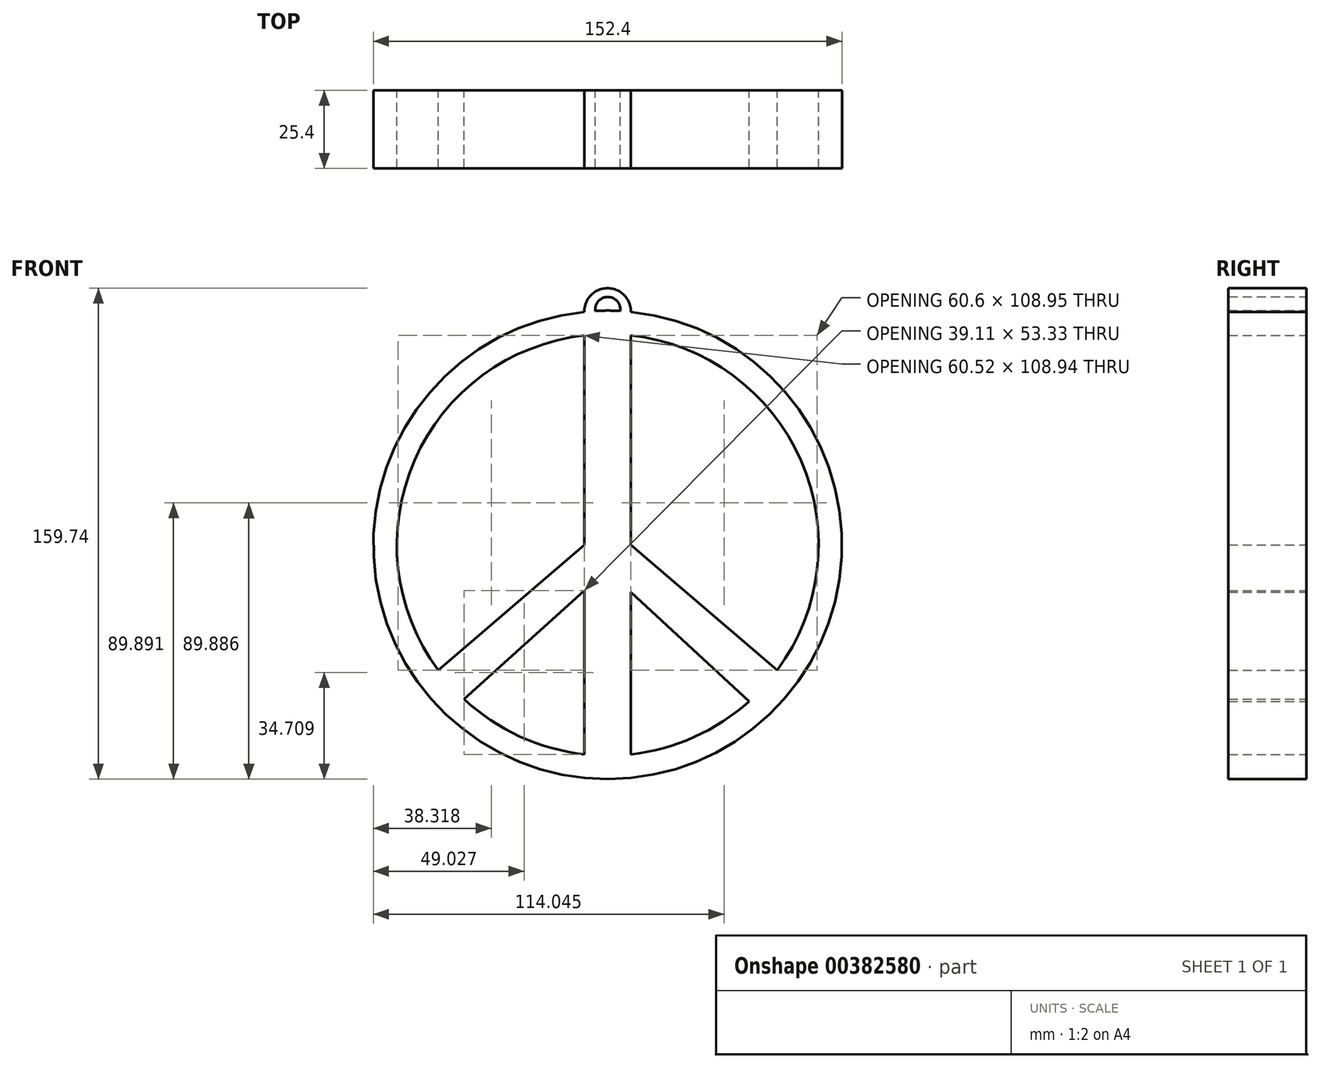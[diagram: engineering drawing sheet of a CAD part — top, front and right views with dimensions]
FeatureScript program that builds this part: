
annotation { "Feature Type Name" : "Feature", "Feature Type Description" : "" }
export const myFeature = defineFeature(function(context is Context, id is Id, definition is map)
    precondition{}
    {
        {
            var Q0;
            Q0=qCreatedBy(makeId("Front.planeOp"),FACE);
            var sketch = newSketch(context, id + "F0", { "sketchPlane" : qUnion([Q0])});
            skArc(sketch, "E0", {"start": v(-7.62, 75.82) * mm, "mid": v(0.04, -76.2) * mm, "end": v(7.54, 75.83) * mm});
            skLineSegment(sketch, "E1", {"start": v(7.54, 68.16) * mm, "end": v(7.54, 0) * mm});
            skLineSegment(sketch, "E2", {"start": v(-7.62, 68.16) * mm, "end": v(-7.62, 0) * mm});
            skLineSegment(sketch, "E3", {"start": v(-7.62, 0) * mm, "end": v(-55.14, -40.78) * mm});
            skLineSegment(sketch, "E4", {"start": v(55.14, -40.78) * mm, "end": v(7.54, 0) * mm});
            skLineSegment(sketch, "E5.trimOffspring", {"start": v(7.54, -15.38) * mm, "end": v(7.54, -68.16) * mm});
            skLineSegment(sketch, "E6.trimOffspring", {"start": v(-7.62, -14.83) * mm, "end": v(-7.62, -68.16) * mm});
            skArc(sketch, "E7", {"start": v(-46.73, -50.2) * mm, "mid": v(-28.62, -62.32) * mm, "end": v(-7.62, -68.16) * mm});
            skArc(sketch, "E8.trimOffspring", {"start": v(7.54, -68.16) * mm, "mid": v(28.1, -62.56) * mm, "end": v(45.95, -50.91) * mm});
            skArc(sketch, "E9.trimOffspring", {"start": v(55.14, -40.78) * mm, "mid": v(62.85, 27.45) * mm, "end": v(7.54, 68.16) * mm});
            skArc(sketch, "E10.trimOffspring", {"start": v(-7.62, 68.16) * mm, "mid": v(-62.86, 27.42) * mm, "end": v(-55.14, -40.78) * mm});
            skLineSegment(sketch, "E11", {"start": v(-7.62, -14.83) * mm, "end": v(-46.73, -50.2) * mm});
            skLineSegment(sketch, "E12", {"start": v(7.54, -15.38) * mm, "end": v(45.95, -50.91) * mm});
            skArc(sketch, "E13", {"start": v(7.54, 75.83) * mm, "mid": v(-0.04, 83.54) * mm, "end": v(-7.62, 75.82) * mm});
            skArc(sketch, "E14", {"start": v(4.06, 76.1) * mm, "mid": v(0.04, 80.7) * mm, "end": v(-4, 76.1) * mm});
            skArc(sketch, "E15", {"start": v(4.06, 76.1) * mm, "mid": v(0.03, 76.25) * mm, "end": v(-4, 76.1) * mm});
            skSolve(sketch);
        }
        {
            var Q0;
            Q0=makeQuery(id+"F0.imprint","IMPRINT",FACE,{"disambiguationData":[TD([[makeQuery(id+"F0.imprint","IMPRINT",EDGE,{"derivedFrom":sQuery(id+"F0.wireOp",EDGE,"E0")}),1.0]])]});
            extrude(context, id + "F1", {"entities" : qUnion([Q0]), "offsetDistance" : 25.4 * mm, "depth" : 25.4 * mm});
        }
    });
